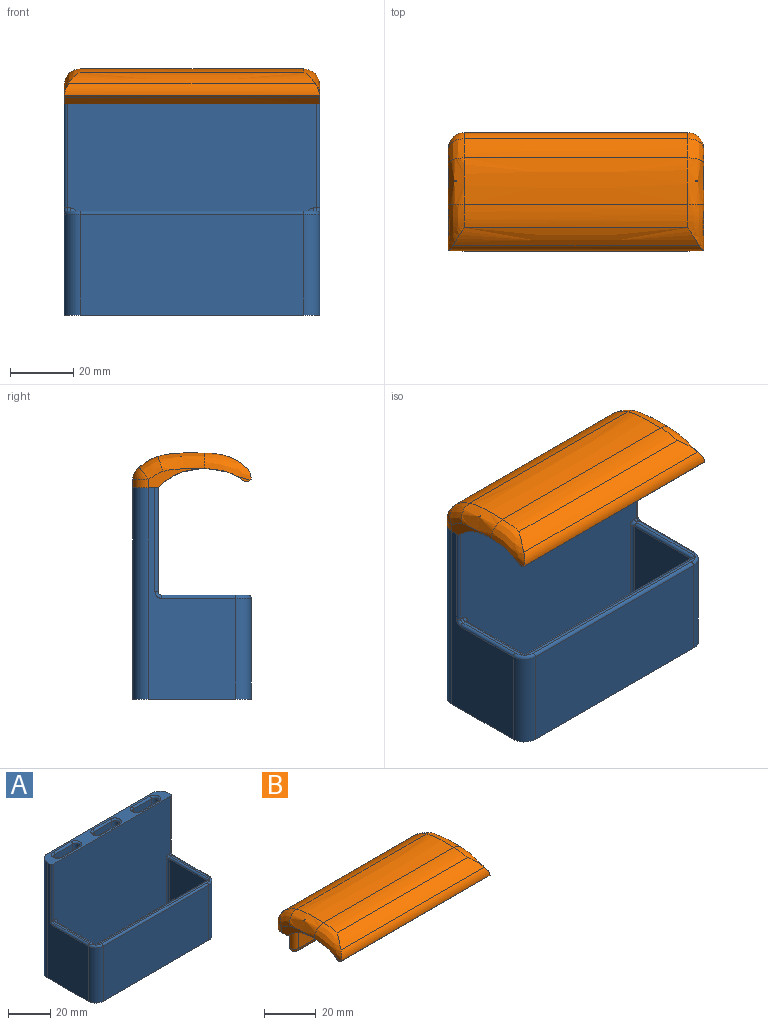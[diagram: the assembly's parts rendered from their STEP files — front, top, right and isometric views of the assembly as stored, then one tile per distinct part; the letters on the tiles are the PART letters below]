
ASSEMBLY  parts=2 mates=1
PART A: 67 faces, bbox 81.8x37.9x67 mm
  f0: plane 26.15x1mm, normal (0,0,1), area 25.3mm2, adj f39,f41,f46,f47
  f1: plane 76.29x1mm, normal (0,0,1), area 74.6mm2, adj f45,f46,f49,f50
  f2: plane 81x8mm, normal (0,0,1), area 336mm2, adj f12,f14,f16,f17,f33,f34,f37,f43
  f3: cylinder r=3mm len=6mm, axis (0,0,-1), area 28.3mm2, adj f4,f6,f7,f8
  f4: plane 11x3mm, normal (0,-1,0), area 33mm2, adj f3,f5,f7,f8
  f5: cylinder r=3mm len=6mm, axis (0,0,-1), area 28.3mm2, adj f4,f6,f7,f8
  f6: plane 11x3mm, normal (0,1,0), area 33mm2, adj f3,f5,f7,f8
  f7: plane 75x26.5mm, normal (0,0,1), area 1892.8mm2, adj f3,f4,f5,f6,f9,f10,f11,f16
  f8: plane 81x37.5mm, normal (0,0,-1), area 2921.8mm2, adj f3,f4,f5,f6,f12,f13,f14,f17
  f9: plane 29x25.5mm, normal (1,0,0), area 739.5mm2, adj f7,f10,f40,f47
  f10: plane 75x29mm, normal (0,1,0), area 2175mm2, adj f7,f9,f11,f50
  f11: plane 29x25.5mm, normal (-1,0,0), area 739.5mm2, adj f7,f10,f52,f54
  f12: plane 67x27.5mm, normal (-1,0,0), area 950.9mm2, adj f2,f8,f34,f35,f37,f38,f41
  f13: plane 71x32mm, normal (0,-1,0), area 2272mm2, adj f8,f35,f36,f45
  f14: plane 67x27.5mm, normal (1,0,0), area 950.9mm2, adj f2,f8,f33,f36,f43,f44,f48
  f15: plane 26.15x1mm, normal (0,0,1), area 25.3mm2, adj f44,f49,f51,f52
  f16: plane 79x64mm, normal (0,-1,0), area 4871.7mm2, adj f2,f7,f37,f39,f40,f42,f43,f51
  f17: plane 71x67mm, normal (0,1,0), area 4757mm2, adj f2,f8,f33,f34
  f18: cylinder r=2mm len=12mm, axis (0,0,1), area 75.4mm2, adj f19,f21,f22,f65
  f19: plane 12x12mm, normal (0,-1,0), area 144mm2, adj f18,f20,f22,f63
  f20: cylinder r=2mm len=12mm, axis (0,0,1), area 75.4mm2, adj f19,f21,f22,f64
  f21: plane 12x12mm, normal (0,1,0), area 144mm2, adj f18,f20,f22,f66
  f22: plane 16x4mm, normal (0,0,1), area 60.6mm2, adj f18,f19,f20,f21
  f23: plane 12x12mm, normal (0,-1,0), area 144mm2, adj f24,f26,f27,f59
  f24: cylinder r=2mm len=12mm, axis (0,0,1), area 75.4mm2, adj f23,f25,f27,f60
  f25: plane 12x12mm, normal (0,1,0), area 144mm2, adj f24,f26,f27,f62
  f26: cylinder r=2mm len=12mm, axis (0,0,1), area 75.4mm2, adj f23,f25,f27,f61
  f27: plane 16x4mm, normal (0,0,1), area 60.6mm2, adj f23,f24,f25,f26
  f28: plane 12x12mm, normal (0,-1,0), area 144mm2, adj f29,f31,f32,f57
  f29: cylinder r=2mm len=12mm, axis (0,0,1), area 75.4mm2, adj f28,f30,f32,f55
  f30: plane 12x12mm, normal (0,1,0), area 144mm2, adj f29,f31,f32,f56
  f31: cylinder r=2mm len=12mm, axis (0,0,1), area 75.4mm2, adj f28,f30,f32,f58
  f32: plane 16x4mm, normal (0,0,1), area 60.6mm2, adj f28,f29,f30,f31
  f33: cylinder r=5mm len=67mm, axis (0,0,-1), area 526.2mm2, adj f2,f8,f14,f17
  f34: cylinder r=5mm len=67mm, axis (0,0,1), area 526.2mm2, adj f2,f8,f12,f17
  f35: cylinder r=5mm len=32mm, axis (0,0,-1), area 251.3mm2, adj f8,f12,f13,f46
  f36: cylinder r=5mm len=32mm, axis (0,0,1), area 251.3mm2, adj f8,f13,f14,f49
  f37: cylinder r=1mm len=33mm, axis (0,0,1), area 51.8mm2, adj f2,f12,f16,f38
  f38: torus R=2mm, axis (1,0,0), area 3.4mm2, adj f12,f37,f39,f41
  f39: cylinder r=1mm len=1mm, axis (1,0,0), area 1.6mm2, adj f0,f16,f38,f42
  f40: cylinder r=1mm len=29mm, axis (0,0,1), area 45.6mm2, adj f7,f9,f16,f42
  f41: cylinder r=1mm len=23.5mm, axis (0,1,0), area 36.9mm2, adj f0,f12,f38,f46
  f42: torus R=2mm, axis (0,-1,0), area 3.4mm2, adj f16,f39,f40,f47
  f43: cylinder r=1mm len=33mm, axis (0,0,-1), area 51.8mm2, adj f2,f14,f16,f48
  f44: cylinder r=1mm len=23.5mm, axis (0,-1,0), area 36.9mm2, adj f14,f15,f48,f49
  f45: cylinder r=1mm len=71mm, axis (-1,0,0), area 111.5mm2, adj f1,f13,f46,f49
  f46: torus R=4mm, axis (0,0,1), area 11.4mm2, adj f0,f1,f35,f41,f45,f47,f50
  f47: cylinder r=1mm len=26.4mm, axis (0,-1,0), area 40.6mm2, adj f0,f9,f42,f46,f50
  f48: torus R=2mm, axis (1,0,0), area 3.4mm2, adj f14,f43,f44,f51
  f49: torus R=4mm, axis (0,0,1), area 11.4mm2, adj f1,f15,f36,f44,f45,f50,f52
  f50: cylinder r=1mm len=76.8mm, axis (1,0,0), area 118.9mm2, adj f1,f10,f46,f47,f49,f52
  f51: cylinder r=1mm len=1mm, axis (-1,0,0), area 1.6mm2, adj f15,f16,f48,f53
  f52: cylinder r=1mm len=26.4mm, axis (0,1,0), area 40.6mm2, adj f11,f15,f49,f50,f53
  f53: torus R=2mm, axis (0,-1,0), area 3.4mm2, adj f16,f51,f52,f54
  f54: cylinder r=1mm len=29mm, axis (0,0,-1), area 45.6mm2, adj f7,f11,f16,f53
  f55: torus R=3mm, axis (0,0,1), area 11.7mm2, adj f2,f29,f56,f57
  f56: cylinder r=1mm len=12mm, axis (-1,0,0), area 18.8mm2, adj f2,f30,f55,f58
  f57: cylinder r=1mm len=12mm, axis (1,0,0), area 18.8mm2, adj f2,f28,f55,f58
  f58: torus R=3mm, axis (0,0,1), area 11.7mm2, adj f2,f31,f56,f57
  f59: cylinder r=1mm len=12mm, axis (1,0,0), area 18.8mm2, adj f2,f23,f60,f61
  f60: torus R=3mm, axis (0,0,1), area 11.7mm2, adj f2,f24,f59,f62
  f61: torus R=3mm, axis (0,0,1), area 11.7mm2, adj f2,f26,f59,f62
  f62: cylinder r=1mm len=12mm, axis (-1,0,0), area 18.8mm2, adj f2,f25,f60,f61
  f63: cylinder r=1mm len=12mm, axis (1,0,0), area 18.8mm2, adj f2,f19,f64,f65
  f64: torus R=3mm, axis (0,0,1), area 11.7mm2, adj f2,f20,f63,f66
  f65: torus R=3mm, axis (0,0,1), area 11.7mm2, adj f2,f18,f63,f66
  f66: cylinder r=1mm len=12mm, axis (-1,0,0), area 18.8mm2, adj f2,f21,f64,f65
PART B: 49 faces, bbox 81x41.2x24.1 mm
  f0: plane 4.44x1.83mm, normal (1,0,0), area 2.1mm2, adj f1,f47,f48
  f1: cylinder r=2mm len=81mm, axis (-1,0,0), area 253mm2, adj f0,f2,f3,f46,f47,f48
  f2: plane 4.44x1.83mm, normal (-1,0,0), area 2.1mm2, adj f1,f3,f48
  f3: bspline ~18.85x9.5mm, area 98.8mm2, adj f1,f2,f4,f43,f44,f45,f46,f48
  f4: extruded ~81x14.75mm, area 1211.9mm2, adj f3,f5,f41,f42,f47,f48
  f5: extruded ~81x7.38mm, area 728.6mm2, adj f4,f6,f41,f42
  f6: plane 81x8mm, normal (0,0,-1), area 455.6mm2, adj f5,f7,f11,f12,f13,f14,f18,f19
  f7: plane 12x11mm, normal (0,1,0), area 132mm2, adj f6,f8,f11,f13
  f8: cylinder r=2mm len=12mm, axis (-1,0,0), area 75.4mm2, adj f7,f9,f10,f12
  f9: sphere r=2mm, area 14.8mm2, adj f8,f13
  f10: sphere r=2mm, area 10.3mm2, adj f8,f11
  f11: cylinder r=2mm len=11mm, axis (0,0,-1), area 69.1mm2, adj f6,f7,f10,f12
  f12: plane 12x11mm, normal (0,-1,0), area 132mm2, adj f6,f8,f11,f13
  f13: cylinder r=2mm len=11mm, axis (0,0,-1), area 69.1mm2, adj f6,f7,f9,f12
  f14: plane 12x11mm, normal (0,1,0), area 132mm2, adj f6,f15,f18,f20
  f15: cylinder r=2mm len=12mm, axis (-1,0,0), area 75.4mm2, adj f14,f16,f17,f19
  f16: sphere r=2mm, area 14.8mm2, adj f15,f20
  f17: sphere r=2mm, area 10.3mm2, adj f15,f18
  f18: cylinder r=2mm len=11mm, axis (0,0,-1), area 69.1mm2, adj f6,f14,f17,f19
  f19: plane 12x11mm, normal (0,-1,0), area 132mm2, adj f6,f15,f18,f20
  f20: cylinder r=2mm len=11mm, axis (0,0,-1), area 69.1mm2, adj f6,f14,f16,f19
  f21: cylinder r=5mm len=5mm, axis (0,0,1), area 20.6mm2, adj f6,f22,f33,f41
  f22: sphere r=5mm, area 22.7mm2, adj f21,f23,f31
  f23: cylinder r=5mm len=71mm, axis (-1,0,0), area 322.4mm2, adj f22,f24,f30,f33
  f24: sphere r=5mm, area 22.7mm2, adj f23,f25,f32
  f25: bspline ~10.46x8.66mm, area 50.2mm2, adj f24,f26,f30,f42
  f26: bspline ~21.34x7.03mm, area 112mm2, adj f25,f27,f28,f29,f42,f47
  f27: extruded ~77.33x0.13mm, area 10.5mm2, adj f26,f28,f43
  f28: plane 77.33x0.13mm, normal (0,-0.32,-0.95), area 10.5mm2, adj f26,f27,f43
  f29: extruded ~71x14.75mm, area 1054.7mm2, adj f26,f30,f43,f44
  f30: extruded ~71x6.08mm, area 498.3mm2, adj f23,f25,f29,f31
  f31: bspline ~10.46x8.66mm, area 50.2mm2, adj f22,f30,f41,f43
  f32: cylinder r=5mm len=5mm, axis (0,0,-1), area 20.6mm2, adj f6,f24,f33,f42
  f33: plane 71x2.62mm, normal (0,1,0), area 185.9mm2, adj f6,f21,f23,f32
  f34: plane 12x11mm, normal (0,-1,0), area 132mm2, adj f6,f35,f38,f40
  f35: cylinder r=2mm len=12mm, axis (-1,0,0), area 75.4mm2, adj f34,f36,f37,f39
  f36: sphere r=2mm, area 8mm2, adj f35,f38
  f37: sphere r=2mm, area 10.3mm2, adj f35,f40
  f38: cylinder r=2mm len=11mm, axis (0,0,-1), area 69.1mm2, adj f6,f34,f36,f39
  f39: plane 12x11mm, normal (0,1,0), area 132mm2, adj f6,f35,f38,f40
  f40: cylinder r=2mm len=11mm, axis (0,0,-1), area 69.1mm2, adj f6,f34,f37,f39
  f41: plane 17.76x6.14mm, normal (-1,0,0), area 33.7mm2, adj f4,f5,f6,f21,f31,f43
  f42: plane 17.82x6.14mm, normal (1,0,0), area 33.7mm2, adj f4,f5,f6,f25,f26,f32,f47
  f43: bspline ~21.34x7.03mm, area 112.1mm2, adj f3,f27,f28,f29,f31,f41
  f44: extruded ~71x7.38mm, area 531.2mm2, adj f3,f29,f45,f47
  f45: extruded ~78.05x5.69mm, area 497.8mm2, adj f3,f44,f46,f47
  f46: cylinder r=5mm len=80.94mm, axis (-1,0,0), area 336.5mm2, adj f1,f3,f45,f47
  f47: bspline ~18.92x9.4mm, area 98.8mm2, adj f0,f1,f4,f26,f42,f44,f45,f46
  f48: extruded ~81x4.58mm, area 424.8mm2, adj f0,f1,f2,f3,f4,f47
PLACE A t=(-34.5,-10.45,13.22)mm fixed
PLACE B t=(-34.5,-10.45,13.22)mm
MATE slider B.f6 <-> A.f2  axis (0,0,-1) through (-17.02,26.86,80.22)mm
